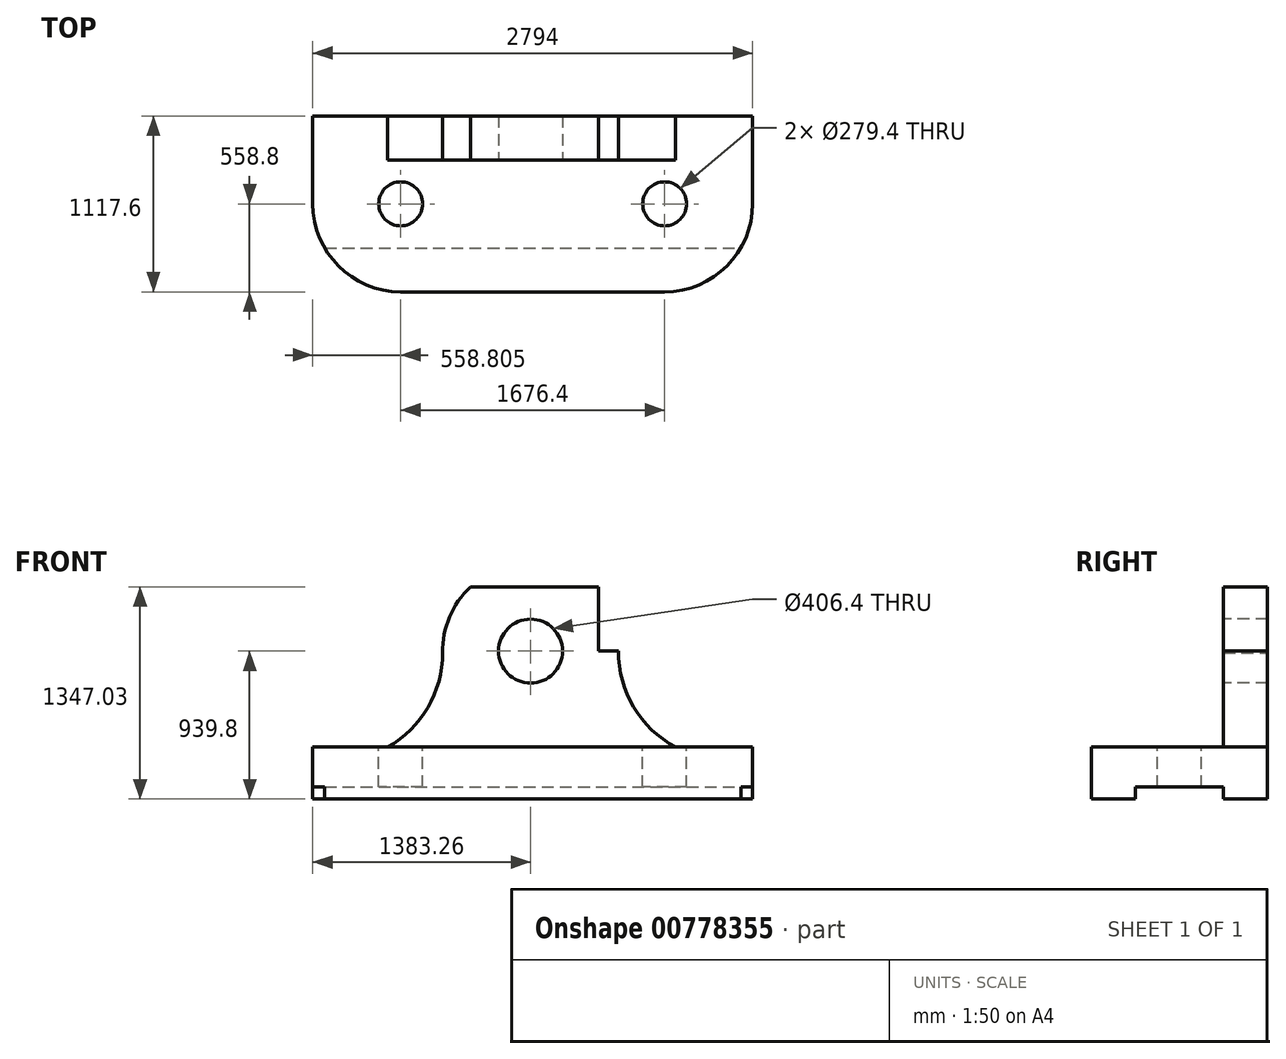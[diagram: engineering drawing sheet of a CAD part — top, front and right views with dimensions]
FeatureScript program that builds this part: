
annotation { "Feature Type Name" : "Feature", "Feature Type Description" : "" }
export const myFeature = defineFeature(function(context is Context, id is Id, definition is map)
    precondition{}
    {
        {
            var Q0;
            Q0=qCreatedBy(makeId("Front.planeOp"),FACE);
            var sketch = newSketch(context, id + "F0", { "sketchPlane" : qUnion([Q0])});
            skLineSegment(sketch, "E0", {"start": v(-1656.66, 0) * mm, "end": v(1137.34, 0) * mm});
            skLineSegment(sketch, "E1", {"start": v(-1656.66, 0) * mm, "end": v(-1656.66, 330.2) * mm});
            skLineSegment(sketch, "E2", {"start": v(-1656.66, 330.2) * mm, "end": v(-703.95, 330.2) * mm});
            skLineSegment(sketch, "E3", {"start": v(-703.95, 330.2) * mm, "end": v(-703.95, 1340.68) * mm});
            skLineSegment(sketch, "E4", {"start": v(-697.6, 1347.03) * mm, "end": v(157.15, 1347.03) * mm});
            skLineSegment(sketch, "E5", {"start": v(157.15, 1347.03) * mm, "end": v(157.15, 330.2) * mm});
            skLineSegment(sketch, "E6", {"start": v(157.15, 330.2) * mm, "end": v(1137.34, 330.2) * mm});
            skLineSegment(sketch, "E7", {"start": v(1137.34, 330.2) * mm, "end": v(1137.34, 0) * mm});
            skPoint(sketch, "E8.visualSharp", {"position": v(-703.95, 1347.03) * mm});
            skArc(sketch, "E8.filletArc", {"start": v(-697.6, 1347.03) * mm, "mid": v(-702.09, 1345.17) * mm, "end": v(-703.95, 1340.68) * mm});
            skSolve(sketch);
        }
        {
            var Q0;
            Q0=makeQuery(id+"F0.imprint","IMPRINT",FACE,{"disambiguationData":[TD([[makeQuery(id+"F0.imprint","IMPRINT",EDGE,{"derivedFrom":sQuery(id+"F0.wireOp",EDGE,"E0")}),1.0]])]});
            extrude(context, id + "F1", {"entities" : qUnion([Q0]), "depth" : 1117.6 * mm, "offsetDistance" : 25.4 * mm});
        }
        {
            var Q0;
            Q0=makeQuery(id+"F1.opExtrude","CAP_EDGE",EDGE,{"disambiguationData":[OSD([sQuery(id+"F0.wireOp",EDGE,"E1")])],"isStart":false});
            var Q1;
            Q1=makeQuery(id+"F1.opExtrude","CAP_EDGE",EDGE,{"disambiguationData":[OSD([sQuery(id+"F0.wireOp",EDGE,"E7")])],"isStart":false});
            fillet(context, id + "F2", {"entities" : qUnion([Q0, Q1]), "radius" : 76.2 * mm, "tangentPropagation" : true, "allowEdgeOverflow" : false});
        }
        {
            var Q0;
            Q0=makeQuery(id+"F1.opExtrude","SWEPT_FACE",FACE,{"disambiguationData":[OSD([sQuery(id+"F0.wireOp",EDGE,"E5")])]});
            var sketch = newSketch(context, id + "F3", { "sketchPlane" : qUnion([Q0])});
            skLineSegment(sketch, "E9", {"start": v(-1117.6, 330.2) * mm, "end": v(-279.4, 330.2) * mm});
            skLineSegment(sketch, "E10", {"start": v(-279.4, 330.2) * mm, "end": v(-279.4, 1347.03) * mm});
            skLineSegment(sketch, "E11", {"start": v(-279.4, 1347.03) * mm, "end": v(-1117.6, 1347.03) * mm});
            skLineSegment(sketch, "E12", {"start": v(-1117.6, 1347.03) * mm, "end": v(-1117.6, 330.2) * mm});
            skSolve(sketch);
        }
        {
            var Q0;
            Q0=makeQuery(id+"F3.imprint","IMPRINT",FACE,{"disambiguationData":[TD([[makeQuery(id+"F3.imprint","IMPRINT",EDGE,{"derivedFrom":sQuery(id+"F3.wireOp",EDGE,"E9")}),1.0]])]});
            extrude(context, id + "F4", {"entities" : qUnion([Q0]), "operationType" : NewBodyOperationType.REMOVE, "oppositeDirection" : true, "depth" : 889 * mm, "offsetDistance" : 25.4 * mm});
        }
        {
            var Q0;
            Q0=makeQuery(id+"F4.boolean.opBoolean","MERGE",FACE,{"derivedFrom":[makeQuery(id+"F1.opExtrude","SWEPT_FACE",FACE,{"disambiguationData":[OSD([sQuery(id+"F0.wireOp",EDGE,"E2")])]}),makeQuery(id+"F1.opExtrude","SWEPT_FACE",FACE,{"disambiguationData":[OSD([sQuery(id+"F0.wireOp",EDGE,"E6")])]}),makeQuery(id+"F4.opExtrude","SWEPT_FACE",FACE,{"disambiguationData":[OSD([sQuery(id+"F3.wireOp",EDGE,"E9")])]})]});
            var sketch = newSketch(context, id + "F5", { "sketchPlane" : qUnion([Q0])});
            skLineSegment(sketch, "E13", {"start": v(-259.66, -1117.6) * mm, "end": v(-259.66, -558.8) * mm});
            skLineSegment(sketch, "E14", {"start": v(-259.66, -558.8) * mm, "end": v(-1097.86, -558.8) * mm});
            skLineSegment(sketch, "E15", {"start": v(-259.66, -558.8) * mm, "end": v(578.54, -558.8) * mm});
            skCircle(sketch, "E16", {"center": v(-1097.86, -558.8) * mm, "radius": 139.7 * mm});
            skCircle(sketch, "E17", {"center": v(578.54, -558.8) * mm, "radius": 139.7 * mm});
            skSolve(sketch);
        }
        {
            var Q0;
            Q0=makeQuery(id+"F5.imprint","IMPRINT",FACE,{"disambiguationData":[TD([[makeQuery(id+"F5.imprint","IMPRINT",EDGE,{"derivedFrom":sQuery(id+"F5.wireOp",EDGE,"E17")}),1.0]])]});
            var Q1;
            Q1=makeQuery(id+"F5.imprint","IMPRINT",FACE,{"disambiguationData":[TD([[makeQuery(id+"F5.imprint","IMPRINT",EDGE,{"derivedFrom":sQuery(id+"F5.wireOp",EDGE,"E16")}),1.0]])]});
            extrude(context, id + "F6", {"entities" : qUnion([Q0, Q1]), "operationType" : NewBodyOperationType.REMOVE, "oppositeDirection" : true, "depth" : 330.2 * mm, "offsetDistance" : 25.4 * mm});
        }
        {
            var Q0;
            Q0=makeQuery(id+"F4.boolean.opBoolean","MERGE",FACE,{"derivedFrom":[makeQuery(id+"F1.opExtrude","SWEPT_FACE",FACE,{"disambiguationData":[OSD([sQuery(id+"F0.wireOp",EDGE,"E2")])]}),makeQuery(id+"F1.opExtrude","SWEPT_FACE",FACE,{"disambiguationData":[OSD([sQuery(id+"F0.wireOp",EDGE,"E6")])]}),makeQuery(id+"F4.opExtrude","SWEPT_FACE",FACE,{"disambiguationData":[OSD([sQuery(id+"F3.wireOp",EDGE,"E9")])]})]});
            var sketch = newSketch(context, id + "F7", { "sketchPlane" : qUnion([Q0])});
            skCircle(sketch, "E18", {"center": v(-1097.86, -558.8) * mm, "radius": 558.8 * mm});
            skCircle(sketch, "E19", {"center": v(578.54, -558.8) * mm, "radius": 558.8 * mm});
            skSolve(sketch);
        }
        {
            var Q0;
            {var subQ1=sQuery(id+"F0.wireOp",EDGE,"E2");var subQ2=sQuery(id+"F0.wireOp",EDGE,"E1");var subQ7=makeQuery(id+"F2.opFillet","BLEND_EDGE",EDGE,{"blendedFrom":[makeQuery(id+"F1.opExtrude","CAP_EDGE",EDGE,{"disambiguationData":[OSD([subQ2])],"isStart":false}),makeQuery(id+"F1.opExtrude","SWEPT_FACE",FACE,{"disambiguationData":[OSD([subQ1])]})],"blendedInto":[makeQuery(id+"F1.opExtrude","SWEPT_FACE",FACE,{"disambiguationData":[OSD([subQ1])]})]});Q0=makeQuery(id+"F7.imprint","IMPRINT",FACE,{"disambiguationData":[TD([[makeQuery(id+"F7.imprint","IMPRINT",EDGE,{"derivedFrom":subQ7}),1.0]])]});}
            var Q1;
            {var subQ1=sQuery(id+"F0.wireOp",EDGE,"E7");var subQ2=sQuery(id+"F0.wireOp",EDGE,"E6");var subQ7=makeQuery(id+"F2.opFillet","BLEND_EDGE",EDGE,{"blendedFrom":[makeQuery(id+"F1.opExtrude","CAP_EDGE",EDGE,{"disambiguationData":[OSD([subQ1])],"isStart":false}),makeQuery(id+"F1.opExtrude","SWEPT_FACE",FACE,{"disambiguationData":[OSD([subQ2])]})],"blendedInto":[makeQuery(id+"F1.opExtrude","SWEPT_FACE",FACE,{"disambiguationData":[OSD([subQ2])]})]});Q1=makeQuery(id+"F7.imprint","IMPRINT",FACE,{"disambiguationData":[TD([[makeQuery(id+"F7.imprint","IMPRINT",EDGE,{"derivedFrom":subQ7}),1.0]])]});}
            extrude(context, id + "F8", {"entities" : qUnion([Q0, Q1]), "operationType" : NewBodyOperationType.REMOVE, "oppositeDirection" : true, "depth" : 330.2 * mm, "offsetDistance" : 25.4 * mm});
        }
        {
            var Q0;
            Q0=makeQuery(id+"F4.boolean.opBoolean","COPY",FACE,{"derivedFrom":makeQuery(id+"F4.opExtrude","SWEPT_FACE",FACE,{"disambiguationData":[OSD([sQuery(id+"F3.wireOp",EDGE,"E10")])]})});
            var sketch = newSketch(context, id + "F9", { "sketchPlane" : qUnion([Q0])});
            skLineSegment(sketch, "E20", {"start": v(-273.4, 330.2) * mm, "end": v(-273.4, 939.8) * mm});
            skCircle(sketch, "E21", {"center": v(-273.4, 939.8) * mm, "radius": 558.8 * mm});
            skSolve(sketch);
        }
        {
            var Q0;
            {var subQ1=sQuery(id+"F3.wireOp",EDGE,"E10");var subQ4=makeQuery(id+"F4.opExtrude","SWEPT_FACE",FACE,{"disambiguationData":[OSD([subQ1])]});var subQ7=makeQuery(id+"F4.boolean.opBoolean","INTERSECT",EDGE,{"derivedFrom":[makeQuery(id+"F1.opExtrude","SWEPT_FACE",FACE,{"disambiguationData":[OSD([sQuery(id+"F0.wireOp",EDGE,"E8.filletArc")])]}),subQ4]});Q0=makeQuery(id+"F9.imprint","IMPRINT",FACE,{"disambiguationData":[TD([[makeQuery(id+"F9.imprint","IMPRINT",EDGE,{"derivedFrom":subQ7}),-1.0]])]});}
            var Q1;
            {var subQ0=sQuery(id+"F9.wireOp",EDGE,"E21");var subQ1=sQuery(id+"F3.wireOp",EDGE,"E10");var subQ4=makeQuery(id+"F4.boolean.opBoolean","COPY",EDGE,{"derivedFrom":makeQuery(id+"F4.opExtrude","CAP_EDGE",EDGE,{"disambiguationData":[OSD([subQ1])],"isStart":true})});var subQ5=makeQuery(id+"F9.imprint","INTERSECT",VERTEX,{"disambiguationData":[OD(0.0)],"derivedFrom":[subQ4,subQ0]});Q1=makeQuery(id+"F9.imprint","IMPRINT",FACE,{"disambiguationData":[TD([[makeQuery(id+"F9.imprint","IMPRINT",EDGE,{"disambiguationData":[TD([[subQ5,-1.0]])],"derivedFrom":subQ0}),-1.0]])]});}
            extrude(context, id + "F10", {"entities" : qUnion([Q0, Q1]), "operationType" : NewBodyOperationType.REMOVE, "oppositeDirection" : true, "depth" : 279.4 * mm, "offsetDistance" : 25.4 * mm});
        }
        {
            var Q0;
            Q0=makeQuery(id+"F4.boolean.opBoolean","COPY",FACE,{"derivedFrom":makeQuery(id+"F4.opExtrude","SWEPT_FACE",FACE,{"disambiguationData":[OSD([sQuery(id+"F3.wireOp",EDGE,"E10")])]})});
            var sketch = newSketch(context, id + "F11", { "sketchPlane" : qUnion([Q0])});
            skLineSegment(sketch, "E22", {"start": v(-273.4, 330.2) * mm, "end": v(-273.4, 939.8) * mm});
            skCircle(sketch, "E23", {"center": v(-273.4, 939.8) * mm, "radius": 558.8 * mm});
            skSolve(sketch);
        }
        {
            var Q0;
            {var subQ1=makeQuery(id+"F4.boolean.opBoolean","COPY",EDGE,{"derivedFrom":makeQuery(id+"F4.opExtrude","SWEPT_EDGE",EDGE,{"disambiguationData":[OSD([sQuery(id+"F0.wireOp",EDGE,"E4"),sQuery(id+"F0.wireOp",EDGE,"E5"),sQuery(id+"F3.wireOp",EDGE,"E10"),sQuery(id+"F3.wireOp",EDGE,"E11")])]})});Q0=makeQuery(id+"F11.imprint","IMPRINT",FACE,{"disambiguationData":[TD([[makeQuery(id+"F11.imprint","IMPRINT",EDGE,{"derivedFrom":subQ1}),1.0]])]});}
            var Q1;
            {var subQ0=sQuery(id+"F11.wireOp",EDGE,"E23");var subQ1=makeQuery(id+"F4.boolean.opBoolean","COPY",EDGE,{"derivedFrom":makeQuery(id+"F4.opExtrude","CAP_EDGE",EDGE,{"disambiguationData":[OSD([sQuery(id+"F3.wireOp",EDGE,"E10")])],"isStart":true})});var subQ2=makeQuery(id+"F11.imprint","INTERSECT",VERTEX,{"disambiguationData":[OD(0.0)],"derivedFrom":[subQ1,subQ0]});Q1=makeQuery(id+"F11.imprint","IMPRINT",FACE,{"disambiguationData":[TD([[makeQuery(id+"F11.imprint","IMPRINT",EDGE,{"disambiguationData":[TD([[subQ2,1.0]])],"derivedFrom":subQ0}),1.0]])]});}
            var Q2;
            {var subQ0=sQuery(id+"F11.wireOp",EDGE,"E23");var subQ1=makeQuery(id+"F4.boolean.opBoolean","INTERSECT",EDGE,{"derivedFrom":[makeQuery(id+"F1.opExtrude","SWEPT_FACE",FACE,{"disambiguationData":[OSD([sQuery(id+"F0.wireOp",EDGE,"E3")])]}),makeQuery(id+"F4.opExtrude","SWEPT_FACE",FACE,{"disambiguationData":[OSD([sQuery(id+"F3.wireOp",EDGE,"E10")])]})]});var subQ2=makeQuery(id+"F11.imprint","INTERSECT",VERTEX,{"disambiguationData":[OD(0.0)],"derivedFrom":[subQ1,subQ0]});Q2=makeQuery(id+"F11.imprint","IMPRINT",FACE,{"disambiguationData":[TD([[makeQuery(id+"F11.imprint","IMPRINT",EDGE,{"disambiguationData":[TD([[subQ2,-1.0]])],"derivedFrom":subQ0}),1.0]])]});}
            extrude(context, id + "F12", {"entities" : qUnion([Q0, Q1, Q2]), "operationType" : NewBodyOperationType.ADD, "oppositeDirection" : true, "depth" : 279.4 * mm, "offsetDistance" : 25.4 * mm});
        }
        {
            var Q0;
            {var subQ0=sQuery(id+"F11.wireOp",EDGE,"E23");var subQ1=sQuery(id+"F3.wireOp",EDGE,"E10");Q0=makeQuery(id+"F12.boolean.opBoolean","MERGE",FACE,{"derivedFrom":[makeQuery(id+"F4.boolean.opBoolean","COPY",FACE,{"derivedFrom":makeQuery(id+"F4.opExtrude","SWEPT_FACE",FACE,{"disambiguationData":[OSD([subQ1])]})}),makeQuery(id+"F12.opExtrude","CAP_FACE",FACE,{"disambiguationData":[OSD([sQuery(id+"F0.wireOp",EDGE,"E4"),sQuery(id+"F0.wireOp",EDGE,"E5"),subQ1,sQuery(id+"F3.wireOp",EDGE,"E11"),subQ0])],"isStart":true}),makeQuery(id+"F12.opExtrude","CAP_FACE",FACE,{"disambiguationData":[OSD([sQuery(id+"F0.wireOp",EDGE,"E3"),subQ1,subQ0])],"isStart":true}),makeQuery(id+"F12.opExtrude","CAP_FACE",FACE,{"disambiguationData":[OSD([subQ1,subQ0])],"isStart":true})]});}
            var sketch = newSketch(context, id + "F13", { "sketchPlane" : qUnion([Q0])});
            skCircle(sketch, "E24", {"center": v(-273.4, 939.8) * mm, "radius": 203.2 * mm});
            skSolve(sketch);
        }
        {
            var Q0;
            Q0=makeQuery(id+"F13.imprint","IMPRINT",FACE,{"disambiguationData":[TD([[makeQuery(id+"F13.imprint","IMPRINT",EDGE,{"derivedFrom":sQuery(id+"F13.wireOp",EDGE,"E24")}),1.0]])]});
            extrude(context, id + "F14", {"entities" : qUnion([Q0]), "operationType" : NewBodyOperationType.REMOVE, "oppositeDirection" : true, "depth" : 279.4 * mm, "offsetDistance" : 25.4 * mm});
        }
        {
            var Q0;
            {var subQ0=sQuery(id+"F11.wireOp",EDGE,"E23");var subQ1=sQuery(id+"F3.wireOp",EDGE,"E10");var subQ2=sQuery(id+"F0.wireOp",EDGE,"E3");var subQ3=sQuery(id+"F0.wireOp",EDGE,"E5");var subQ4=sQuery(id+"F0.wireOp",EDGE,"E4");Q0=makeQuery(id+"F12.boolean.opBoolean","MERGE",FACE,{"derivedFrom":[makeQuery(id+"F1.opExtrude","CAP_FACE",FACE,{"disambiguationData":[OSD([sQuery(id+"F0.wireOp",EDGE,"E0"),sQuery(id+"F0.wireOp",EDGE,"E1"),sQuery(id+"F0.wireOp",EDGE,"E2"),subQ2,subQ4,subQ3,sQuery(id+"F0.wireOp",EDGE,"E6"),sQuery(id+"F0.wireOp",EDGE,"E7"),sQuery(id+"F0.wireOp",EDGE,"E8.filletArc")])],"isStart":true}),makeQuery(id+"F12.opExtrude","CAP_FACE",FACE,{"disambiguationData":[OSD([subQ4,subQ3,subQ1,sQuery(id+"F3.wireOp",EDGE,"E11"),subQ0])],"isStart":false}),makeQuery(id+"F12.opExtrude","CAP_FACE",FACE,{"disambiguationData":[OSD([subQ2,subQ1,subQ0])],"isStart":false}),makeQuery(id+"F12.opExtrude","CAP_FACE",FACE,{"disambiguationData":[OSD([subQ1,subQ0])],"isStart":false})]});}
            var sketch = newSketch(context, id + "F15", { "sketchPlane" : qUnion([Q0])});
            skLineSegment(sketch, "E25", {"start": v(273.4, 939.8) * mm, "end": v(-1330.53, 939.8) * mm});
            skLineSegment(sketch, "E26", {"start": v(273.4, 939.8) * mm, "end": v(1925.29, 939.8) * mm});
            skArc(sketch, "E27", {"start": v(-647.25, 330.2) * mm, "mid": v(-381.45, 584.62) * mm, "end": v(-285.4, 939.8) * mm});
            skArc(sketch, "E28", {"start": v(832.2, 939.8) * mm, "mid": v(922.34, 587.08) * mm, "end": v(1180.3, 330.2) * mm});
            skSolve(sketch);
        }
        {
            var Q0;
            {var subQ9=sQuery(id+"F0.wireOp",EDGE,"E5");var subQ15=makeQuery(id+"F1.opExtrude","CAP_EDGE",EDGE,{"disambiguationData":[OSD([subQ9])],"isStart":true});Q0=makeQuery(id+"F15.imprint","IMPRINT",FACE,{"disambiguationData":[TD([[makeQuery(id+"F15.imprint","IMPRINT",EDGE,{"derivedFrom":subQ15}),-1.0]])]});}
            var Q1;
            {var subQ7=sQuery(id+"F0.wireOp",EDGE,"E3");var subQ15=makeQuery(id+"F1.opExtrude","CAP_EDGE",EDGE,{"disambiguationData":[OSD([subQ7])],"isStart":true});Q1=makeQuery(id+"F15.imprint","IMPRINT",FACE,{"disambiguationData":[TD([[makeQuery(id+"F15.imprint","IMPRINT",EDGE,{"derivedFrom":subQ15}),-1.0]])]});}
            extrude(context, id + "F16", {"entities" : qUnion([Q0, Q1]), "operationType" : NewBodyOperationType.ADD, "oppositeDirection" : true, "depth" : 279.4 * mm, "offsetDistance" : 25.4 * mm});
        }
        {
            var Q0;
            Q0=makeQuery(id+"F1.opExtrude","SWEPT_FACE",FACE,{"disambiguationData":[OSD([sQuery(id+"F0.wireOp",EDGE,"E7")])]});
            var sketch = newSketch(context, id + "F17", { "sketchPlane" : qUnion([Q0])});
            skLineSegment(sketch, "E29", {"start": v(0, 0) * mm, "end": v(-279.4, 0) * mm});
            skLineSegment(sketch, "E30", {"start": v(-279.4, 0) * mm, "end": v(-279.4, 76.2) * mm});
            skLineSegment(sketch, "E31", {"start": v(-279.4, 76.2) * mm, "end": v(-838.2, 76.2) * mm});
            skLineSegment(sketch, "E32", {"start": v(-838.2, 76.2) * mm, "end": v(-838.2, 0) * mm});
            skLineSegment(sketch, "E33", {"start": v(-838.2, 0) * mm, "end": v(-279.4, 0) * mm});
            skSolve(sketch);
        }
        {
            var Q0;
            {var subQ0=sQuery(id+"F17.wireOp",EDGE,"E30");Q0=makeQuery(id+"F17.imprint","IMPRINT",FACE,{"disambiguationData":[TD([[makeQuery(id+"F17.imprint","IMPRINT",EDGE,{"derivedFrom":subQ0}),1.0]])]});}
            var Q1;
            {var subQ0=sQuery(id+"F17.wireOp",EDGE,"E32");Q1=makeQuery(id+"F17.imprint","IMPRINT",FACE,{"disambiguationData":[TD([[makeQuery(id+"F17.imprint","IMPRINT",EDGE,{"derivedFrom":subQ0}),1.0]])]});}
            extrude(context, id + "F18", {"entities" : qUnion([Q0, Q1]), "operationType" : NewBodyOperationType.REMOVE, "oppositeDirection" : true, "depth" : 2794 * mm, "offsetDistance" : 25.4 * mm});
        }
    });
